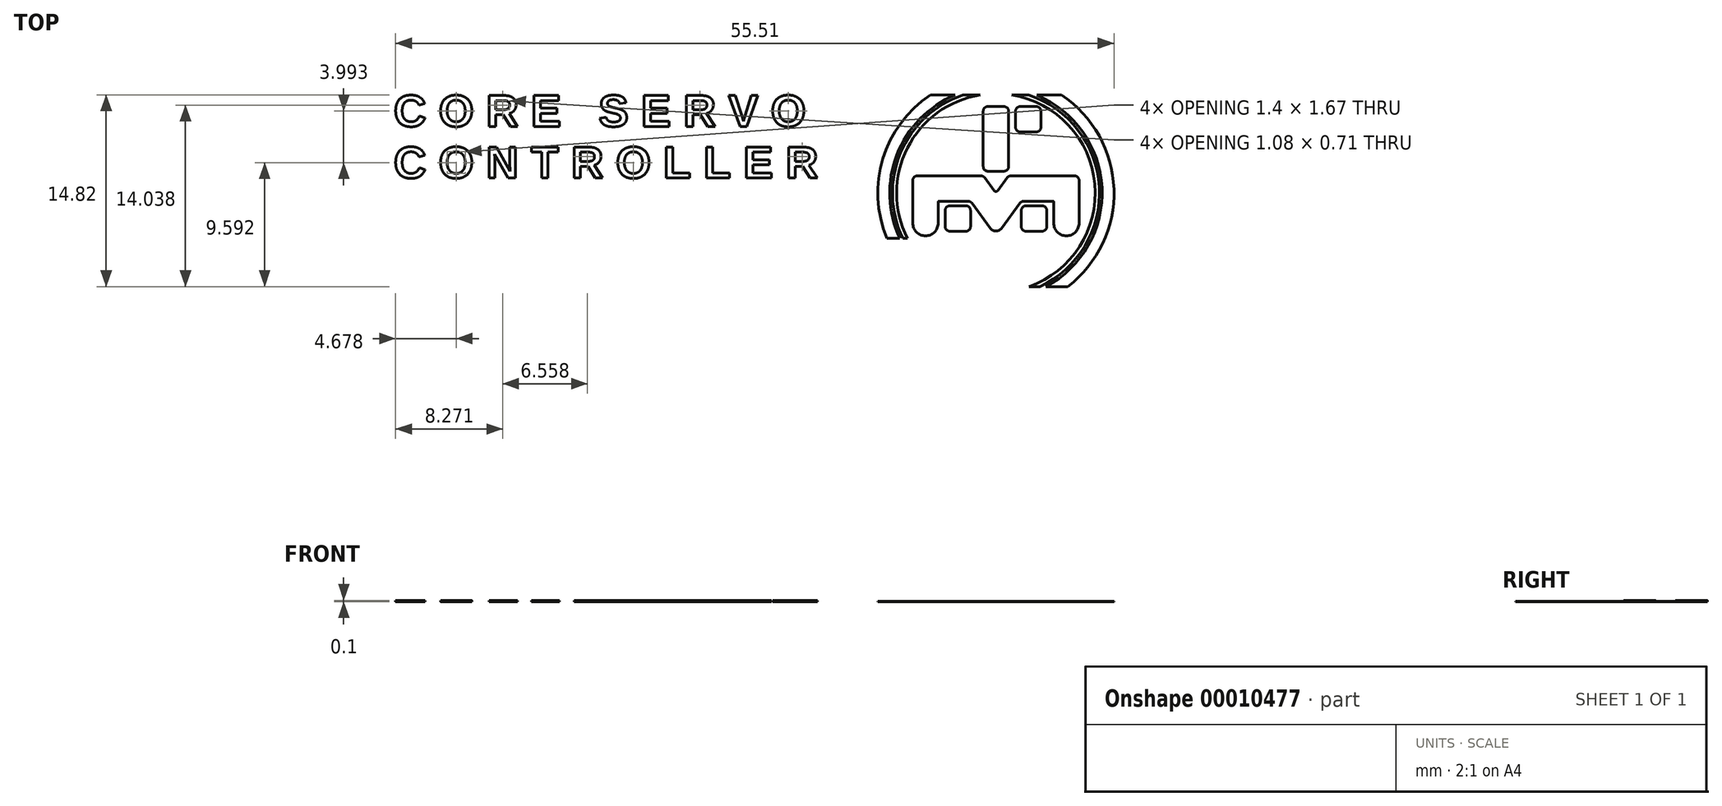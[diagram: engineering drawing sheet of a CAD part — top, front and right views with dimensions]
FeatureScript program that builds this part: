
annotation { "Feature Type Name" : "Feature", "Feature Type Description" : "" }
export const myFeature = defineFeature(function(context is Context, id is Id, definition is map)
    precondition{}
    {
        {
            var Q0;
            Q0=qCreatedBy(makeId("Top.planeOp"),FACE);
            var sketch = newSketch(context, id + "F0", { "sketchPlane" : qUnion([Q0])});
            skLineSegment(sketch, "E0.bottom", {"start": v(62.75, -5.5) * mm, "end": v(66.25, -5.5) * mm});
            skLineSegment(sketch, "E0.top", {"start": v(62.75, -19.5) * mm, "end": v(66.25, -19.5) * mm});
            skLineSegment(sketch, "E0.left", {"start": v(61.75, -6.5) * mm, "end": v(61.75, -18.5) * mm});
            skLineSegment(sketch, "E0.right", {"start": v(67.25, -6.5) * mm, "end": v(67.25, -18.5) * mm});
            skLineSegment(sketch, "E1.bottom", {"start": v(69.75, -5.5) * mm, "end": v(73.25, -5.5) * mm});
            skLineSegment(sketch, "E1.top", {"start": v(69.75, -11) * mm, "end": v(73.25, -11) * mm});
            skLineSegment(sketch, "E1.left", {"start": v(68.75, -6.5) * mm, "end": v(68.75, -10) * mm});
            skLineSegment(sketch, "E1.right", {"start": v(74.25, -6.5) * mm, "end": v(74.25, -10) * mm});
            skLineSegment(sketch, "E2", {"start": v(64.5, -19.5) * mm, "end": v(64.5, -33.5) * mm, "construction": true});
            skLineSegment(sketch, "E3", {"start": v(63.3, -31.86) * mm, "end": v(59.27, -26.4) * mm});
            skLineSegment(sketch, "E4", {"start": v(58.47, -26) * mm, "end": v(52.1, -26) * mm});
            skLineSegment(sketch, "E5", {"start": v(52, -26.1) * mm, "end": v(52, -30.75) * mm});
            skLineSegment(sketch, "E6.0", {"start": v(46.5, -21.5) * mm, "end": v(46.5, -30.75) * mm});
            skLineSegment(sketch, "E6.1", {"start": v(61.24, -20.5) * mm, "end": v(47.5, -20.5) * mm});
            skLineSegment(sketch, "E6.2", {"start": v(64.1, -23.68) * mm, "end": v(62.05, -20.9) * mm});
            skLineSegment(sketch, "E7", {"start": v(49.25, -33.5) * mm, "end": v(49.25, -33.5) * mm});
            skPoint(sketch, "E8.orphan", {"position": v(52, -33.5) * mm});
            skPoint(sketch, "E9.visualSharp", {"position": v(46.5, -33.5) * mm});
            skArc(sketch, "E9.filletArc", {"start": v(46.5, -30.75) * mm, "mid": v(47.3, -32.7) * mm, "end": v(49.25, -33.5) * mm});
            skArc(sketch, "E10.filletArc", {"start": v(49.25, -33.5) * mm, "mid": v(51.2, -32.7) * mm, "end": v(52, -30.75) * mm});
            skLineSegment(sketch, "E11.right", {"start": v(59, -28) * mm, "end": v(59, -31.5) * mm});
            skLineSegment(sketch, "E11.left", {"start": v(53.5, -28) * mm, "end": v(53.5, -31.5) * mm});
            skLineSegment(sketch, "E11.top", {"start": v(54.5, -32.5) * mm, "end": v(58, -32.5) * mm});
            skLineSegment(sketch, "E11.bottom", {"start": v(54.5, -27) * mm, "end": v(58, -27) * mm});
            skPoint(sketch, "E12.0.MirrorP", {"position": v(77, -33.5) * mm});
            skLineSegment(sketch, "E12.1.MirrorCS", {"start": v(74.5, -27) * mm, "end": v(71, -27) * mm});
            skPoint(sketch, "E12.2.MirrorP", {"position": v(82.5, -33.5) * mm});
            skLineSegment(sketch, "E12.3.MirrorCS", {"start": v(70, -28) * mm, "end": v(70, -31.5) * mm});
            skLineSegment(sketch, "E12.4.MirrorCS", {"start": v(75.5, -28) * mm, "end": v(75.5, -31.5) * mm});
            skLineSegment(sketch, "E12.5.MirrorCS", {"start": v(74.5, -32.5) * mm, "end": v(71, -32.5) * mm});
            skLineSegment(sketch, "E12.6.MirrorCS", {"start": v(70.53, -26) * mm, "end": v(76.9, -26) * mm});
            skLineSegment(sketch, "E12.7.MirrorCS", {"start": v(77, -26.1) * mm, "end": v(77, -30.75) * mm});
            skArc(sketch, "E12.8.MirrorCS", {"start": v(79.75, -33.5) * mm, "mid": v(77.8, -32.7) * mm, "end": v(77, -30.75) * mm});
            skLineSegment(sketch, "E12.9.MirrorCS", {"start": v(79.75, -33.5) * mm, "end": v(79.75, -33.5) * mm});
            skLineSegment(sketch, "E12.10.MirrorCS", {"start": v(67.76, -20.5) * mm, "end": v(81.5, -20.5) * mm});
            skPoint(sketch, "E12.11.MirrorP", {"position": v(77, -33.5) * mm});
            skLineSegment(sketch, "E12.12.MirrorCS", {"start": v(64.9, -23.68) * mm, "end": v(66.95, -20.9) * mm});
            skArc(sketch, "E12.13.MirrorCS", {"start": v(82.5, -30.75) * mm, "mid": v(81.7, -32.7) * mm, "end": v(79.75, -33.5) * mm});
            skLineSegment(sketch, "E12.14.MirrorCS", {"start": v(65.7, -31.86) * mm, "end": v(69.73, -26.4) * mm});
            skLineSegment(sketch, "E12.15.MirrorCS", {"start": v(82.5, -21.5) * mm, "end": v(82.5, -30.75) * mm});
            skPoint(sketch, "E13.visualSharp", {"position": v(68.75, -5.5) * mm});
            skArc(sketch, "E13.filletArc", {"start": v(69.75, -5.5) * mm, "mid": v(69.04, -5.8) * mm, "end": v(68.75, -6.5) * mm});
            skPoint(sketch, "E14.visualSharp", {"position": v(74.25, -5.5) * mm});
            skArc(sketch, "E14.filletArc", {"start": v(74.25, -6.5) * mm, "mid": v(73.96, -5.8) * mm, "end": v(73.25, -5.5) * mm});
            skPoint(sketch, "E15.visualSharp", {"position": v(74.25, -11) * mm});
            skArc(sketch, "E15.filletArc", {"start": v(73.25, -11) * mm, "mid": v(73.96, -10.7) * mm, "end": v(74.25, -10) * mm});
            skPoint(sketch, "E16.visualSharp", {"position": v(68.75, -11) * mm});
            skArc(sketch, "E16.filletArc", {"start": v(68.75, -10) * mm, "mid": v(69.04, -10.7) * mm, "end": v(69.75, -11) * mm});
            skPoint(sketch, "E17.visualSharp", {"position": v(67.25, -5.5) * mm});
            skArc(sketch, "E17.filletArc", {"start": v(67.25, -6.5) * mm, "mid": v(66.96, -5.8) * mm, "end": v(66.25, -5.5) * mm});
            skPoint(sketch, "E18.visualSharp", {"position": v(61.75, -5.5) * mm});
            skArc(sketch, "E18.filletArc", {"start": v(62.75, -5.5) * mm, "mid": v(62.04, -5.8) * mm, "end": v(61.75, -6.5) * mm});
            skPoint(sketch, "E19.visualSharp", {"position": v(61.75, -19.5) * mm});
            skArc(sketch, "E19.filletArc", {"start": v(61.75, -18.5) * mm, "mid": v(62.04, -19.2) * mm, "end": v(62.75, -19.5) * mm});
            skPoint(sketch, "E20.visualSharp", {"position": v(67.25, -19.5) * mm});
            skArc(sketch, "E20.filletArc", {"start": v(66.25, -19.5) * mm, "mid": v(66.96, -19.2) * mm, "end": v(67.25, -18.5) * mm});
            skPoint(sketch, "E21.visualSharp", {"position": v(70, -32.5) * mm});
            skArc(sketch, "E21.filletArc", {"start": v(70, -31.5) * mm, "mid": v(70.3, -32.2) * mm, "end": v(71, -32.5) * mm});
            skPoint(sketch, "E22.visualSharp", {"position": v(75.5, -27) * mm});
            skArc(sketch, "E22.filletArc", {"start": v(75.5, -28) * mm, "mid": v(75.2, -27.3) * mm, "end": v(74.5, -27) * mm});
            skPoint(sketch, "E23.visualSharp", {"position": v(70, -27) * mm});
            skArc(sketch, "E23.filletArc", {"start": v(71, -27) * mm, "mid": v(70.3, -27.3) * mm, "end": v(70, -28) * mm});
            skPoint(sketch, "E24.visualSharp", {"position": v(75.5, -32.5) * mm});
            skArc(sketch, "E24.filletArc", {"start": v(74.5, -32.5) * mm, "mid": v(75.2, -32.2) * mm, "end": v(75.5, -31.5) * mm});
            skPoint(sketch, "E25.visualSharp", {"position": v(59, -32.5) * mm});
            skArc(sketch, "E25.filletArc", {"start": v(58, -32.5) * mm, "mid": v(58.7, -32.2) * mm, "end": v(59, -31.5) * mm});
            skPoint(sketch, "E26.visualSharp", {"position": v(59, -27) * mm});
            skArc(sketch, "E26.filletArc", {"start": v(59, -28) * mm, "mid": v(58.7, -27.3) * mm, "end": v(58, -27) * mm});
            skPoint(sketch, "E27.visualSharp", {"position": v(53.5, -27) * mm});
            skArc(sketch, "E27.filletArc", {"start": v(54.5, -27) * mm, "mid": v(53.8, -27.3) * mm, "end": v(53.5, -28) * mm});
            skPoint(sketch, "E28.visualSharp", {"position": v(53.5, -32.5) * mm});
            skArc(sketch, "E28.filletArc", {"start": v(53.5, -31.5) * mm, "mid": v(53.8, -32.2) * mm, "end": v(54.5, -32.5) * mm});
            skPoint(sketch, "E29.visualSharp", {"position": v(46.5, -20.5) * mm});
            skArc(sketch, "E29.filletArc", {"start": v(47.5, -20.5) * mm, "mid": v(46.8, -20.8) * mm, "end": v(46.5, -21.5) * mm});
            skPoint(sketch, "E30.visualSharp", {"position": v(82.5, -20.5) * mm});
            skArc(sketch, "E30.filletArc", {"start": v(82.5, -21.5) * mm, "mid": v(82.2, -20.8) * mm, "end": v(81.5, -20.5) * mm});
            skPoint(sketch, "E31.visualSharp", {"position": v(61.75, -20.5) * mm});
            skArc(sketch, "E31.filletArc", {"start": v(62.05, -20.9) * mm, "mid": v(61.7, -20.6) * mm, "end": v(61.24, -20.5) * mm});
            skPoint(sketch, "E32.visualSharp", {"position": v(67.25, -20.5) * mm});
            skArc(sketch, "E32.filletArc", {"start": v(67.76, -20.5) * mm, "mid": v(67.3, -20.6) * mm, "end": v(66.95, -20.9) * mm});
            skPoint(sketch, "E33.visualSharp", {"position": v(52, -26) * mm});
            skArc(sketch, "E33.filletArc", {"start": v(52.1, -26) * mm, "mid": v(52.03, -26.03) * mm, "end": v(52, -26.1) * mm});
            skPoint(sketch, "E34.visualSharp", {"position": v(77, -26) * mm});
            skArc(sketch, "E34.filletArc", {"start": v(77, -26.1) * mm, "mid": v(76.97, -26.03) * mm, "end": v(76.9, -26) * mm});
            skPoint(sketch, "E35.visualSharp", {"position": v(70.03, -26) * mm});
            skArc(sketch, "E35.filletArc", {"start": v(70.53, -26) * mm, "mid": v(70.08, -26.1) * mm, "end": v(69.73, -26.4) * mm});
            skPoint(sketch, "E36.visualSharp", {"position": v(58.97, -26) * mm});
            skArc(sketch, "E36.filletArc", {"start": v(59.27, -26.4) * mm, "mid": v(58.92, -26.1) * mm, "end": v(58.47, -26) * mm});
            skPoint(sketch, "E37.visualSharp", {"position": v(64.5, -33.5) * mm});
            skArc(sketch, "E37.filletArc", {"start": v(63.3, -31.86) * mm, "mid": v(64.5, -32.47) * mm, "end": v(65.7, -31.86) * mm});
            skPoint(sketch, "E38.visualSharp", {"position": v(64.5, -24.23) * mm});
            skArc(sketch, "E38.filletArc", {"start": v(64.1, -23.68) * mm, "mid": v(64.5, -23.89) * mm, "end": v(64.9, -23.68) * mm});
            skArc(sketch, "E39", {"start": v(71.68, -44.5) * mm, "mid": v(85.92, -22.29) * mm, "end": v(67.92, -3) * mm});
            skArc(sketch, "E40", {"start": v(74, -44.5) * mm, "mid": v(86.85, -22.94) * mm, "end": v(71.6, -3) * mm});
            skArc(sketch, "E41", {"start": v(75.35, -44.5) * mm, "mid": v(87.46, -23.1) * mm, "end": v(73.32, -3) * mm});
            skArc(sketch, "E42", {"start": v(80.06, -44.5) * mm, "mid": v(90.04, -23.4) * mm, "end": v(78.72, -3) * mm});
            skLineSegment(sketch, "E43", {"start": v(80.06, -44.5) * mm, "end": v(75.35, -44.5) * mm});
            skLineSegment(sketch, "E44.trimOffspring", {"start": v(74, -44.5) * mm, "end": v(71.68, -44.5) * mm});
            skLineSegment(sketch, "E45", {"start": v(40.9, -34) * mm, "end": v(43.69, -34) * mm});
            skLineSegment(sketch, "E46.trimOffspring", {"start": v(44.36, -34) * mm, "end": v(45.34, -34) * mm});
            skLineSegment(sketch, "E47", {"start": v(50.28, -3) * mm, "end": v(55.68, -3) * mm});
            skArc(sketch, "E48.trimOffspring", {"start": v(61.08, -3) * mm, "mid": v(45.33, -14.5) * mm, "end": v(45.34, -34) * mm});
            skArc(sketch, "E49.trimOffspring", {"start": v(50.28, -3) * mm, "mid": v(40.05, -16.82) * mm, "end": v(40.9, -34) * mm});
            skArc(sketch, "E50.trimOffspring", {"start": v(55.68, -3) * mm, "mid": v(43.06, -15.94) * mm, "end": v(43.69, -34) * mm});
            skArc(sketch, "E51.trimOffspring", {"start": v(57.4, -3) * mm, "mid": v(43.86, -15.55) * mm, "end": v(44.36, -34) * mm});
            skLineSegment(sketch, "E52.trimOffspring", {"start": v(67.92, -3) * mm, "end": v(71.6, -3) * mm});
            skLineSegment(sketch, "E53.trimOffspring", {"start": v(57.4, -3) * mm, "end": v(61.08, -3) * mm});
            skLineSegment(sketch, "E54.trimOffspring", {"start": v(73.32, -3) * mm, "end": v(78.72, -3) * mm});
            skSolve(sketch);
        }
        {
            var Q0;
            Q0=makeQuery(id+"F0.imprint","IMPRINT",FACE,{"disambiguationData":[TD([[makeQuery(id+"F0.imprint","IMPRINT",EDGE,{"derivedFrom":sQuery(id+"F0.wireOp",EDGE,"46c11c21-c6ca-42b8-9659-15b4f280ee3c.sketch_text.stroke-197")}),1.0]])]});
            var Q1;
            Q1=makeQuery(id+"F0.imprint","IMPRINT",FACE,{"disambiguationData":[TD([[makeQuery(id+"F0.imprint","IMPRINT",EDGE,{"derivedFrom":sQuery(id+"F0.wireOp",EDGE,"E1.bottom")}),-1.0]])]});
            var Q2;
            Q2=makeQuery(id+"F0.imprint","IMPRINT",FACE,{"disambiguationData":[TD([[makeQuery(id+"F0.imprint","IMPRINT",EDGE,{"derivedFrom":sQuery(id+"F0.wireOp",EDGE,"46c11c21-c6ca-42b8-9659-15b4f280ee3c.sketch_text.stroke-126")}),-1.0]])]});
            var Q3;
            Q3=makeQuery(id+"F0.imprint","IMPRINT",FACE,{"disambiguationData":[TD([[makeQuery(id+"F0.imprint","IMPRINT",EDGE,{"derivedFrom":sQuery(id+"F0.wireOp",EDGE,"46c11c21-c6ca-42b8-9659-15b4f280ee3c.sketch_text.stroke-360")}),-1.0]])]});
            var Q4;
            Q4=makeQuery(id+"F0.imprint","IMPRINT",FACE,{"disambiguationData":[TD([[makeQuery(id+"F0.imprint","IMPRINT",EDGE,{"derivedFrom":sQuery(id+"F0.wireOp",EDGE,"E0.bottom")}),-1.0]])]});
            var Q5;
            Q5=makeQuery(id+"F0.imprint","IMPRINT",FACE,{"disambiguationData":[TD([[makeQuery(id+"F0.imprint","IMPRINT",EDGE,{"derivedFrom":sQuery(id+"F0.wireOp",EDGE,"46c11c21-c6ca-42b8-9659-15b4f280ee3c.sketch_text.stroke-0")}),-1.0]])]});
            var Q6;
            Q6=makeQuery(id+"F0.imprint","IMPRINT",FACE,{"disambiguationData":[TD([[makeQuery(id+"F0.imprint","IMPRINT",EDGE,{"derivedFrom":sQuery(id+"F0.wireOp",EDGE,"46c11c21-c6ca-42b8-9659-15b4f280ee3c.sketch_text.stroke-90")}),-1.0]])]});
            var Q7;
            Q7=makeQuery(id+"F0.imprint","IMPRINT",FACE,{"disambiguationData":[TD([[makeQuery(id+"F0.imprint","IMPRINT",EDGE,{"derivedFrom":sQuery(id+"F0.wireOp",EDGE,"46c11c21-c6ca-42b8-9659-15b4f280ee3c.sketch_text.stroke-145")}),-1.0]])]});
            var Q8;
            Q8=makeQuery(id+"F0.imprint","IMPRINT",FACE,{"disambiguationData":[TD([[makeQuery(id+"F0.imprint","IMPRINT",EDGE,{"derivedFrom":sQuery(id+"F0.wireOp",EDGE,"46c11c21-c6ca-42b8-9659-15b4f280ee3c.sketch_text.stroke-126")}),1.0]])]});
            var Q9;
            Q9=makeQuery(id+"F0.imprint","IMPRINT",FACE,{"disambiguationData":[TD([[makeQuery(id+"F0.imprint","IMPRINT",EDGE,{"derivedFrom":sQuery(id+"F0.wireOp",EDGE,"46c11c21-c6ca-42b8-9659-15b4f280ee3c.sketch_text.stroke-48")}),-1.0]])]});
            var Q10;
            Q10=makeQuery(id+"F0.imprint","IMPRINT",FACE,{"disambiguationData":[TD([[makeQuery(id+"F0.imprint","IMPRINT",EDGE,{"derivedFrom":sQuery(id+"F0.wireOp",EDGE,"46c11c21-c6ca-42b8-9659-15b4f280ee3c.sketch_text.stroke-239")}),1.0]])]});
            var Q11;
            Q11=makeQuery(id+"F0.imprint","IMPRINT",FACE,{"disambiguationData":[TD([[makeQuery(id+"F0.imprint","IMPRINT",EDGE,{"derivedFrom":sQuery(id+"F0.wireOp",EDGE,"E12.1.MirrorCS")}),1.0]])]});
            var Q12;
            Q12=makeQuery(id+"F0.imprint","IMPRINT",FACE,{"disambiguationData":[TD([[makeQuery(id+"F0.imprint","IMPRINT",EDGE,{"derivedFrom":sQuery(id+"F0.wireOp",EDGE,"46c11c21-c6ca-42b8-9659-15b4f280ee3c.sketch_text.stroke-300")}),-1.0]])]});
            var Q13;
            Q13=makeQuery(id+"F0.imprint","IMPRINT",FACE,{"disambiguationData":[TD([[makeQuery(id+"F0.imprint","IMPRINT",EDGE,{"derivedFrom":sQuery(id+"F0.wireOp",EDGE,"46c11c21-c6ca-42b8-9659-15b4f280ee3c.sketch_text.stroke-245")}),-1.0]])]});
            var Q14;
            Q14=makeQuery(id+"F0.imprint","IMPRINT",FACE,{"disambiguationData":[TD([[makeQuery(id+"F0.imprint","IMPRINT",EDGE,{"derivedFrom":sQuery(id+"F0.wireOp",EDGE,"46c11c21-c6ca-42b8-9659-15b4f280ee3c.sketch_text.stroke-268")}),-1.0]])]});
            var Q15;
            Q15=makeQuery(id+"F0.imprint","IMPRINT",FACE,{"disambiguationData":[TD([[makeQuery(id+"F0.imprint","IMPRINT",EDGE,{"derivedFrom":sQuery(id+"F0.wireOp",EDGE,"46c11c21-c6ca-42b8-9659-15b4f280ee3c.sketch_text.stroke-189")}),-1.0]])]});
            var Q16;
            Q16=makeQuery(id+"F0.imprint","IMPRINT",FACE,{"disambiguationData":[TD([[makeQuery(id+"F0.imprint","IMPRINT",EDGE,{"derivedFrom":sQuery(id+"F0.wireOp",EDGE,"46c11c21-c6ca-42b8-9659-15b4f280ee3c.sketch_text.stroke-114")}),-1.0]])]});
            var Q17;
            Q17=makeQuery(id+"F0.imprint","IMPRINT",FACE,{"disambiguationData":[TD([[makeQuery(id+"F0.imprint","IMPRINT",EDGE,{"derivedFrom":sQuery(id+"F0.wireOp",EDGE,"E3")}),-1.0]])]});
            var Q18;
            Q18=makeQuery(id+"F0.imprint","IMPRINT",FACE,{"disambiguationData":[TD([[makeQuery(id+"F0.imprint","IMPRINT",EDGE,{"derivedFrom":sQuery(id+"F0.wireOp",EDGE,"46c11c21-c6ca-42b8-9659-15b4f280ee3c.sketch_text.stroke-345")}),-1.0]])]});
            var Q19;
            Q19=makeQuery(id+"F0.imprint","IMPRINT",FACE,{"disambiguationData":[TD([[makeQuery(id+"F0.imprint","IMPRINT",EDGE,{"derivedFrom":sQuery(id+"F0.wireOp",EDGE,"46c11c21-c6ca-42b8-9659-15b4f280ee3c.sketch_text.stroke-232")}),1.0]])]});
            var Q20;
            Q20=makeQuery(id+"F0.imprint","IMPRINT",FACE,{"disambiguationData":[TD([[makeQuery(id+"F0.imprint","IMPRINT",EDGE,{"derivedFrom":sQuery(id+"F0.wireOp",EDGE,"46c11c21-c6ca-42b8-9659-15b4f280ee3c.sketch_text.stroke-280")}),1.0]])]});
            var Q21;
            Q21=makeQuery(id+"F0.imprint","IMPRINT",FACE,{"disambiguationData":[TD([[makeQuery(id+"F0.imprint","IMPRINT",EDGE,{"derivedFrom":sQuery(id+"F0.wireOp",EDGE,"46c11c21-c6ca-42b8-9659-15b4f280ee3c.sketch_text.stroke-161")}),-1.0]])]});
            var Q22;
            Q22=makeQuery(id+"F0.imprint","IMPRINT",FACE,{"disambiguationData":[TD([[makeQuery(id+"F0.imprint","IMPRINT",EDGE,{"derivedFrom":sQuery(id+"F0.wireOp",EDGE,"46c11c21-c6ca-42b8-9659-15b4f280ee3c.sketch_text.stroke-157")}),-1.0]])]});
            var Q23;
            Q23=makeQuery(id+"F0.imprint","IMPRINT",FACE,{"disambiguationData":[TD([[makeQuery(id+"F0.imprint","IMPRINT",EDGE,{"derivedFrom":sQuery(id+"F0.wireOp",EDGE,"46c11c21-c6ca-42b8-9659-15b4f280ee3c.sketch_text.stroke-84")}),1.0]])]});
            var Q24;
            Q24=makeQuery(id+"F0.imprint","IMPRINT",FACE,{"disambiguationData":[TD([[makeQuery(id+"F0.imprint","IMPRINT",EDGE,{"derivedFrom":sQuery(id+"F0.wireOp",EDGE,"46c11c21-c6ca-42b8-9659-15b4f280ee3c.sketch_text.stroke-60")}),-1.0]])]});
            var Q25;
            Q25=makeQuery(id+"F0.imprint","IMPRINT",FACE,{"disambiguationData":[TD([[makeQuery(id+"F0.imprint","IMPRINT",EDGE,{"derivedFrom":sQuery(id+"F0.wireOp",EDGE,"46c11c21-c6ca-42b8-9659-15b4f280ee3c.sketch_text.stroke-340")}),1.0]])]});
            var Q26;
            Q26=makeQuery(id+"F0.imprint","IMPRINT",FACE,{"disambiguationData":[TD([[makeQuery(id+"F0.imprint","IMPRINT",EDGE,{"derivedFrom":sQuery(id+"F0.wireOp",EDGE,"46c11c21-c6ca-42b8-9659-15b4f280ee3c.sketch_text.stroke-220")}),-1.0]])]});
            var Q27;
            Q27=makeQuery(id+"F0.imprint","IMPRINT",FACE,{"disambiguationData":[TD([[makeQuery(id+"F0.imprint","IMPRINT",EDGE,{"derivedFrom":sQuery(id+"F0.wireOp",EDGE,"46c11c21-c6ca-42b8-9659-15b4f280ee3c.sketch_text.stroke-76")}),-1.0]])]});
            var Q28;
            Q28=makeQuery(id+"F0.imprint","IMPRINT",FACE,{"disambiguationData":[TD([[makeQuery(id+"F0.imprint","IMPRINT",EDGE,{"derivedFrom":sQuery(id+"F0.wireOp",EDGE,"46c11c21-c6ca-42b8-9659-15b4f280ee3c.sketch_text.stroke-327")}),1.0]])]});
            var Q29;
            Q29=makeQuery(id+"F0.imprint","IMPRINT",FACE,{"disambiguationData":[TD([[makeQuery(id+"F0.imprint","IMPRINT",EDGE,{"derivedFrom":sQuery(id+"F0.wireOp",EDGE,"46c11c21-c6ca-42b8-9659-15b4f280ee3c.sketch_text.stroke-29")}),-1.0]])]});
            var Q30;
            Q30=makeQuery(id+"F0.imprint","IMPRINT",FACE,{"disambiguationData":[TD([[makeQuery(id+"F0.imprint","IMPRINT",EDGE,{"derivedFrom":sQuery(id+"F0.wireOp",EDGE,"46c11c21-c6ca-42b8-9659-15b4f280ee3c.sketch_text.stroke-60")}),1.0]])]});
            var Q31;
            Q31=makeQuery(id+"F0.imprint","IMPRINT",FACE,{"disambiguationData":[TD([[makeQuery(id+"F0.imprint","IMPRINT",EDGE,{"derivedFrom":sQuery(id+"F0.wireOp",EDGE,"46c11c21-c6ca-42b8-9659-15b4f280ee3c.sketch_text.stroke-333")}),-1.0]])]});
            var Q32;
            Q32=makeQuery(id+"F0.imprint","IMPRINT",FACE,{"disambiguationData":[TD([[makeQuery(id+"F0.imprint","IMPRINT",EDGE,{"derivedFrom":sQuery(id+"F0.wireOp",EDGE,"E11.right")}),-1.0]])]});
            var Q33;
            Q33=makeQuery(id+"F0.imprint","IMPRINT",FACE,{"disambiguationData":[TD([[makeQuery(id+"F0.imprint","IMPRINT",EDGE,{"derivedFrom":sQuery(id+"F0.wireOp",EDGE,"46c11c21-c6ca-42b8-9659-15b4f280ee3c.sketch_text.stroke-216")}),-1.0]])]});
            var Q34;
            Q34=makeQuery(id+"F0.imprint","IMPRINT",FACE,{"disambiguationData":[TD([[makeQuery(id+"F0.imprint","IMPRINT",EDGE,{"derivedFrom":sQuery(id+"F0.wireOp",EDGE,"46c11c21-c6ca-42b8-9659-15b4f280ee3c.sketch_text.stroke-260")}),-1.0]])]});
            var Q35;
            Q35=makeQuery(id+"F0.imprint","IMPRINT",FACE,{"disambiguationData":[TD([[makeQuery(id+"F0.imprint","IMPRINT",EDGE,{"derivedFrom":sQuery(id+"F0.wireOp",EDGE,"46c11c21-c6ca-42b8-9659-15b4f280ee3c.sketch_text.stroke-286")}),-1.0]])]});
            var Q36;
            Q36=makeQuery(id+"F0.imprint","IMPRINT",FACE,{"disambiguationData":[TD([[makeQuery(id+"F0.imprint","IMPRINT",EDGE,{"derivedFrom":sQuery(id+"F0.wireOp",EDGE,"46c11c21-c6ca-42b8-9659-15b4f280ee3c.sketch_text.stroke-197")}),-1.0]])]});
            var Q37;
            Q37=makeQuery(id+"F0.imprint","IMPRINT",FACE,{"disambiguationData":[TD([[makeQuery(id+"F0.imprint","IMPRINT",EDGE,{"derivedFrom":sQuery(id+"F0.wireOp",EDGE,"46c11c21-c6ca-42b8-9659-15b4f280ee3c.sketch_text.stroke-319")}),-1.0]])]});
            var Q38;
            Q38=makeQuery(id+"F0.imprint","IMPRINT",FACE,{"disambiguationData":[TD([[makeQuery(id+"F0.imprint","IMPRINT",EDGE,{"derivedFrom":sQuery(id+"F0.wireOp",EDGE,"46c11c21-c6ca-42b8-9659-15b4f280ee3c.sketch_text.stroke-366")}),-1.0]])]});
            var Q39;
            Q39=makeQuery(id+"F0.imprint","IMPRINT",FACE,{"disambiguationData":[TD([[makeQuery(id+"F0.imprint","IMPRINT",EDGE,{"derivedFrom":sQuery(id+"F0.wireOp",EDGE,"46c11c21-c6ca-42b8-9659-15b4f280ee3c.sketch_text.stroke-272")}),-1.0]])]});
            var Q40;
            Q40=makeQuery(id+"F0.imprint","IMPRINT",FACE,{"disambiguationData":[TD([[makeQuery(id+"F0.imprint","IMPRINT",EDGE,{"derivedFrom":sQuery(id+"F0.wireOp",EDGE,"46c11c21-c6ca-42b8-9659-15b4f280ee3c.sketch_text.stroke-15")}),-1.0]])]});
            var Q41;
            Q41=makeQuery(id+"F0.imprint","IMPRINT",FACE,{"disambiguationData":[TD([[makeQuery(id+"F0.imprint","IMPRINT",EDGE,{"derivedFrom":sQuery(id+"F0.wireOp",EDGE,"46c11c21-c6ca-42b8-9659-15b4f280ee3c.sketch_text.stroke-168")}),-1.0]])]});
            var Q42;
            Q42=makeQuery(id+"F0.imprint","IMPRINT",FACE,{"disambiguationData":[TD([[makeQuery(id+"F0.imprint","IMPRINT",EDGE,{"derivedFrom":sQuery(id+"F0.wireOp",EDGE,"46c11c21-c6ca-42b8-9659-15b4f280ee3c.sketch_text.stroke-95")}),-1.0]])]});
            var Q43;
            Q43=makeQuery(id+"F0.imprint","IMPRINT",FACE,{"disambiguationData":[TD([[makeQuery(id+"F0.imprint","IMPRINT",EDGE,{"derivedFrom":sQuery(id+"F0.wireOp",EDGE,"46c11c21-c6ca-42b8-9659-15b4f280ee3c.sketch_text.stroke-225")}),-1.0]])]});
            var Q44;
            Q44=makeQuery(id+"F0.imprint","IMPRINT",FACE,{"disambiguationData":[TD([[makeQuery(id+"F0.imprint","IMPRINT",EDGE,{"derivedFrom":sQuery(id+"F0.wireOp",EDGE,"46c11c21-c6ca-42b8-9659-15b4f280ee3c.sketch_text.stroke-231")}),-1.0]])]});
            var Q45;
            Q45=makeQuery(id+"F0.imprint","IMPRINT",FACE,{"disambiguationData":[TD([[makeQuery(id+"F0.imprint","IMPRINT",EDGE,{"derivedFrom":sQuery(id+"F0.wireOp",EDGE,"46c11c21-c6ca-42b8-9659-15b4f280ee3c.sketch_text.stroke-177")}),-1.0]])]});
            var Q46;
            Q46=makeQuery(id+"F0.imprint","IMPRINT",FACE,{"disambiguationData":[TD([[makeQuery(id+"F0.imprint","IMPRINT",EDGE,{"derivedFrom":sQuery(id+"F0.wireOp",EDGE,"E41")}),-1.0]])]});
            var Q47;
            Q47=makeQuery(id+"F0.imprint","IMPRINT",FACE,{"disambiguationData":[TD([[makeQuery(id+"F0.imprint","IMPRINT",EDGE,{"derivedFrom":sQuery(id+"F0.wireOp",EDGE,"E39")}),-1.0]])]});
            var Q48;
            Q48=makeQuery(id+"F0.imprint","IMPRINT",FACE,{"disambiguationData":[TD([[makeQuery(id+"F0.imprint","IMPRINT",EDGE,{"derivedFrom":sQuery(id+"F0.wireOp",EDGE,"E45")}),1.0]])]});
            var Q49;
            Q49=makeQuery(id+"F0.imprint","IMPRINT",FACE,{"disambiguationData":[TD([[makeQuery(id+"F0.imprint","IMPRINT",EDGE,{"derivedFrom":sQuery(id+"F0.wireOp",EDGE,"E46.trimOffspring")}),1.0]])]});
            extrude(context, id + "F1", {"entities" : qUnion([Q0, Q1, Q2, Q3, Q4, Q5, Q6, Q7, Q8, Q9, Q10, Q11, Q12, Q13, Q14, Q15, Q16, Q17, Q18, Q19, Q20, Q21, Q22, Q23, Q24, Q25, Q26, Q27, Q28, Q29, Q30, Q31, Q32, Q33, Q34, Q35, Q36, Q37, Q38, Q39, Q40, Q41, Q42, Q43, Q44, Q45, Q46, Q47, Q48, Q49]), "depth" : .1 * mm});
        }
        {
            var Q0;
            Q0=makeQuery(id+"F1.opExtrude","SWEPT_BODY",BODY,{"disambiguationData":[OSD([sQuery(id+"F0.wireOp",EDGE,"46c11c21-c6ca-42b8-9659-15b4f280ee3c.sketch_text.stroke-149"),sQuery(id+"F0.wireOp",EDGE,"46c11c21-c6ca-42b8-9659-15b4f280ee3c.sketch_text.stroke-150"),sQuery(id+"F0.wireOp",EDGE,"46c11c21-c6ca-42b8-9659-15b4f280ee3c.sketch_text.stroke-151"),sQuery(id+"F0.wireOp",EDGE,"46c11c21-c6ca-42b8-9659-15b4f280ee3c.sketch_text.stroke-152"),sQuery(id+"F0.wireOp",EDGE,"46c11c21-c6ca-42b8-9659-15b4f280ee3c.sketch_text.stroke-153"),sQuery(id+"F0.wireOp",EDGE,"46c11c21-c6ca-42b8-9659-15b4f280ee3c.sketch_text.stroke-154"),sQuery(id+"F0.wireOp",EDGE,"46c11c21-c6ca-42b8-9659-15b4f280ee3c.sketch_text.stroke-155"),sQuery(id+"F0.wireOp",EDGE,"46c11c21-c6ca-42b8-9659-15b4f280ee3c.sketch_text.stroke-156"),sQuery(id+"F0.wireOp",EDGE,"46c11c21-c6ca-42b8-9659-15b4f280ee3c.sketch_text.stroke-157"),sQuery(id+"F0.wireOp",EDGE,"46c11c21-c6ca-42b8-9659-15b4f280ee3c.sketch_text.stroke-158"),sQuery(id+"F0.wireOp",EDGE,"46c11c21-c6ca-42b8-9659-15b4f280ee3c.sketch_text.stroke-159"),sQuery(id+"F0.wireOp",EDGE,"46c11c21-c6ca-42b8-9659-15b4f280ee3c.sketch_text.stroke-160"),sQuery(id+"F0.wireOp",EDGE,"46c11c21-c6ca-42b8-9659-15b4f280ee3c.sketch_text.stroke-161"),sQuery(id+"F0.wireOp",EDGE,"46c11c21-c6ca-42b8-9659-15b4f280ee3c.sketch_text.stroke-162")])]});
            var Q1;
            Q1=makeQuery(id+"F1.opExtrude","SWEPT_BODY",BODY,{"disambiguationData":[OSD([sQuery(id+"F0.wireOp",EDGE,"46c11c21-c6ca-42b8-9659-15b4f280ee3c.sketch_text.stroke-134"),sQuery(id+"F0.wireOp",EDGE,"46c11c21-c6ca-42b8-9659-15b4f280ee3c.sketch_text.stroke-135"),sQuery(id+"F0.wireOp",EDGE,"46c11c21-c6ca-42b8-9659-15b4f280ee3c.sketch_text.stroke-136"),sQuery(id+"F0.wireOp",EDGE,"46c11c21-c6ca-42b8-9659-15b4f280ee3c.sketch_text.stroke-137"),sQuery(id+"F0.wireOp",EDGE,"46c11c21-c6ca-42b8-9659-15b4f280ee3c.sketch_text.stroke-138"),sQuery(id+"F0.wireOp",EDGE,"46c11c21-c6ca-42b8-9659-15b4f280ee3c.sketch_text.stroke-139"),sQuery(id+"F0.wireOp",EDGE,"46c11c21-c6ca-42b8-9659-15b4f280ee3c.sketch_text.stroke-140"),sQuery(id+"F0.wireOp",EDGE,"46c11c21-c6ca-42b8-9659-15b4f280ee3c.sketch_text.stroke-141"),sQuery(id+"F0.wireOp",EDGE,"46c11c21-c6ca-42b8-9659-15b4f280ee3c.sketch_text.stroke-142"),sQuery(id+"F0.wireOp",EDGE,"46c11c21-c6ca-42b8-9659-15b4f280ee3c.sketch_text.stroke-143"),sQuery(id+"F0.wireOp",EDGE,"46c11c21-c6ca-42b8-9659-15b4f280ee3c.sketch_text.stroke-144"),sQuery(id+"F0.wireOp",EDGE,"46c11c21-c6ca-42b8-9659-15b4f280ee3c.sketch_text.stroke-145"),sQuery(id+"F0.wireOp",EDGE,"46c11c21-c6ca-42b8-9659-15b4f280ee3c.sketch_text.stroke-146"),sQuery(id+"F0.wireOp",EDGE,"46c11c21-c6ca-42b8-9659-15b4f280ee3c.sketch_text.stroke-147"),sQuery(id+"F0.wireOp",EDGE,"46c11c21-c6ca-42b8-9659-15b4f280ee3c.sketch_text.stroke-148")])]});
            var Q2;
            Q2=makeQuery(id+"F1.opExtrude","SWEPT_BODY",BODY,{"disambiguationData":[OSD([sQuery(id+"F0.wireOp",EDGE,"46c11c21-c6ca-42b8-9659-15b4f280ee3c.sketch_text.stroke-101"),sQuery(id+"F0.wireOp",EDGE,"46c11c21-c6ca-42b8-9659-15b4f280ee3c.sketch_text.stroke-102"),sQuery(id+"F0.wireOp",EDGE,"46c11c21-c6ca-42b8-9659-15b4f280ee3c.sketch_text.stroke-103"),sQuery(id+"F0.wireOp",EDGE,"46c11c21-c6ca-42b8-9659-15b4f280ee3c.sketch_text.stroke-104"),sQuery(id+"F0.wireOp",EDGE,"46c11c21-c6ca-42b8-9659-15b4f280ee3c.sketch_text.stroke-105"),sQuery(id+"F0.wireOp",EDGE,"46c11c21-c6ca-42b8-9659-15b4f280ee3c.sketch_text.stroke-106"),sQuery(id+"F0.wireOp",EDGE,"46c11c21-c6ca-42b8-9659-15b4f280ee3c.sketch_text.stroke-107"),sQuery(id+"F0.wireOp",EDGE,"46c11c21-c6ca-42b8-9659-15b4f280ee3c.sketch_text.stroke-108"),sQuery(id+"F0.wireOp",EDGE,"46c11c21-c6ca-42b8-9659-15b4f280ee3c.sketch_text.stroke-109"),sQuery(id+"F0.wireOp",EDGE,"46c11c21-c6ca-42b8-9659-15b4f280ee3c.sketch_text.stroke-110"),sQuery(id+"F0.wireOp",EDGE,"46c11c21-c6ca-42b8-9659-15b4f280ee3c.sketch_text.stroke-111"),sQuery(id+"F0.wireOp",EDGE,"46c11c21-c6ca-42b8-9659-15b4f280ee3c.sketch_text.stroke-112"),sQuery(id+"F0.wireOp",EDGE,"46c11c21-c6ca-42b8-9659-15b4f280ee3c.sketch_text.stroke-113"),sQuery(id+"F0.wireOp",EDGE,"46c11c21-c6ca-42b8-9659-15b4f280ee3c.sketch_text.stroke-114")])]});
            var Q3;
            Q3=makeQuery(id+"F1.opExtrude","SWEPT_BODY",BODY,{"disambiguationData":[OSD([sQuery(id+"F0.wireOp",EDGE,"46c11c21-c6ca-42b8-9659-15b4f280ee3c.sketch_text.stroke-79"),sQuery(id+"F0.wireOp",EDGE,"46c11c21-c6ca-42b8-9659-15b4f280ee3c.sketch_text.stroke-80"),sQuery(id+"F0.wireOp",EDGE,"46c11c21-c6ca-42b8-9659-15b4f280ee3c.sketch_text.stroke-81"),sQuery(id+"F0.wireOp",EDGE,"46c11c21-c6ca-42b8-9659-15b4f280ee3c.sketch_text.stroke-82"),sQuery(id+"F0.wireOp",EDGE,"46c11c21-c6ca-42b8-9659-15b4f280ee3c.sketch_text.stroke-83"),sQuery(id+"F0.wireOp",EDGE,"46c11c21-c6ca-42b8-9659-15b4f280ee3c.sketch_text.stroke-84"),sQuery(id+"F0.wireOp",EDGE,"46c11c21-c6ca-42b8-9659-15b4f280ee3c.sketch_text.stroke-85"),sQuery(id+"F0.wireOp",EDGE,"46c11c21-c6ca-42b8-9659-15b4f280ee3c.sketch_text.stroke-86"),sQuery(id+"F0.wireOp",EDGE,"46c11c21-c6ca-42b8-9659-15b4f280ee3c.sketch_text.stroke-87"),sQuery(id+"F0.wireOp",EDGE,"46c11c21-c6ca-42b8-9659-15b4f280ee3c.sketch_text.stroke-88"),sQuery(id+"F0.wireOp",EDGE,"46c11c21-c6ca-42b8-9659-15b4f280ee3c.sketch_text.stroke-89"),sQuery(id+"F0.wireOp",EDGE,"46c11c21-c6ca-42b8-9659-15b4f280ee3c.sketch_text.stroke-90"),sQuery(id+"F0.wireOp",EDGE,"46c11c21-c6ca-42b8-9659-15b4f280ee3c.sketch_text.stroke-91"),sQuery(id+"F0.wireOp",EDGE,"46c11c21-c6ca-42b8-9659-15b4f280ee3c.sketch_text.stroke-92")])]});
            var Q4;
            Q4=makeQuery(id+"F1.opExtrude","SWEPT_BODY",BODY,{"disambiguationData":[OSD([sQuery(id+"F0.wireOp",EDGE,"E0.bottom"),sQuery(id+"F0.wireOp",EDGE,"E0.top"),sQuery(id+"F0.wireOp",EDGE,"E0.left"),sQuery(id+"F0.wireOp",EDGE,"E0.right"),sQuery(id+"F0.wireOp",EDGE,"E17.filletArc"),sQuery(id+"F0.wireOp",EDGE,"E18.filletArc"),sQuery(id+"F0.wireOp",EDGE,"E19.filletArc"),sQuery(id+"F0.wireOp",EDGE,"E20.filletArc")])]});
            var Q5;
            Q5=makeQuery(id+"F1.opExtrude","SWEPT_BODY",BODY,{"disambiguationData":[OSD([sQuery(id+"F0.wireOp",EDGE,"46c11c21-c6ca-42b8-9659-15b4f280ee3c.sketch_text.stroke-242"),sQuery(id+"F0.wireOp",EDGE,"46c11c21-c6ca-42b8-9659-15b4f280ee3c.sketch_text.stroke-243"),sQuery(id+"F0.wireOp",EDGE,"46c11c21-c6ca-42b8-9659-15b4f280ee3c.sketch_text.stroke-244"),sQuery(id+"F0.wireOp",EDGE,"46c11c21-c6ca-42b8-9659-15b4f280ee3c.sketch_text.stroke-245"),sQuery(id+"F0.wireOp",EDGE,"46c11c21-c6ca-42b8-9659-15b4f280ee3c.sketch_text.stroke-246"),sQuery(id+"F0.wireOp",EDGE,"46c11c21-c6ca-42b8-9659-15b4f280ee3c.sketch_text.stroke-247"),sQuery(id+"F0.wireOp",EDGE,"46c11c21-c6ca-42b8-9659-15b4f280ee3c.sketch_text.stroke-248"),sQuery(id+"F0.wireOp",EDGE,"46c11c21-c6ca-42b8-9659-15b4f280ee3c.sketch_text.stroke-249"),sQuery(id+"F0.wireOp",EDGE,"46c11c21-c6ca-42b8-9659-15b4f280ee3c.sketch_text.stroke-250"),sQuery(id+"F0.wireOp",EDGE,"46c11c21-c6ca-42b8-9659-15b4f280ee3c.sketch_text.stroke-251"),sQuery(id+"F0.wireOp",EDGE,"46c11c21-c6ca-42b8-9659-15b4f280ee3c.sketch_text.stroke-252"),sQuery(id+"F0.wireOp",EDGE,"46c11c21-c6ca-42b8-9659-15b4f280ee3c.sketch_text.stroke-253"),sQuery(id+"F0.wireOp",EDGE,"46c11c21-c6ca-42b8-9659-15b4f280ee3c.sketch_text.stroke-254"),sQuery(id+"F0.wireOp",EDGE,"46c11c21-c6ca-42b8-9659-15b4f280ee3c.sketch_text.stroke-255"),sQuery(id+"F0.wireOp",EDGE,"46c11c21-c6ca-42b8-9659-15b4f280ee3c.sketch_text.stroke-256"),sQuery(id+"F0.wireOp",EDGE,"46c11c21-c6ca-42b8-9659-15b4f280ee3c.sketch_text.stroke-257"),sQuery(id+"F0.wireOp",EDGE,"46c11c21-c6ca-42b8-9659-15b4f280ee3c.sketch_text.stroke-258"),sQuery(id+"F0.wireOp",EDGE,"46c11c21-c6ca-42b8-9659-15b4f280ee3c.sketch_text.stroke-259"),sQuery(id+"F0.wireOp",EDGE,"46c11c21-c6ca-42b8-9659-15b4f280ee3c.sketch_text.stroke-260")])]});
            var Q6;
            Q6=makeQuery(id+"F1.opExtrude","SWEPT_BODY",BODY,{"disambiguationData":[OSD([sQuery(id+"F0.wireOp",EDGE,"46c11c21-c6ca-42b8-9659-15b4f280ee3c.sketch_text.stroke-230"),sQuery(id+"F0.wireOp",EDGE,"46c11c21-c6ca-42b8-9659-15b4f280ee3c.sketch_text.stroke-231"),sQuery(id+"F0.wireOp",EDGE,"46c11c21-c6ca-42b8-9659-15b4f280ee3c.sketch_text.stroke-232"),sQuery(id+"F0.wireOp",EDGE,"46c11c21-c6ca-42b8-9659-15b4f280ee3c.sketch_text.stroke-233"),sQuery(id+"F0.wireOp",EDGE,"46c11c21-c6ca-42b8-9659-15b4f280ee3c.sketch_text.stroke-234"),sQuery(id+"F0.wireOp",EDGE,"46c11c21-c6ca-42b8-9659-15b4f280ee3c.sketch_text.stroke-235"),sQuery(id+"F0.wireOp",EDGE,"46c11c21-c6ca-42b8-9659-15b4f280ee3c.sketch_text.stroke-236"),sQuery(id+"F0.wireOp",EDGE,"46c11c21-c6ca-42b8-9659-15b4f280ee3c.sketch_text.stroke-237"),sQuery(id+"F0.wireOp",EDGE,"46c11c21-c6ca-42b8-9659-15b4f280ee3c.sketch_text.stroke-238"),sQuery(id+"F0.wireOp",EDGE,"46c11c21-c6ca-42b8-9659-15b4f280ee3c.sketch_text.stroke-239"),sQuery(id+"F0.wireOp",EDGE,"46c11c21-c6ca-42b8-9659-15b4f280ee3c.sketch_text.stroke-240"),sQuery(id+"F0.wireOp",EDGE,"46c11c21-c6ca-42b8-9659-15b4f280ee3c.sketch_text.stroke-241")])]});
            var Q7;
            Q7=makeQuery(id+"F1.opExtrude","SWEPT_BODY",BODY,{"disambiguationData":[OSD([sQuery(id+"F0.wireOp",EDGE,"46c11c21-c6ca-42b8-9659-15b4f280ee3c.sketch_text.stroke-218"),sQuery(id+"F0.wireOp",EDGE,"46c11c21-c6ca-42b8-9659-15b4f280ee3c.sketch_text.stroke-219"),sQuery(id+"F0.wireOp",EDGE,"46c11c21-c6ca-42b8-9659-15b4f280ee3c.sketch_text.stroke-220"),sQuery(id+"F0.wireOp",EDGE,"46c11c21-c6ca-42b8-9659-15b4f280ee3c.sketch_text.stroke-221"),sQuery(id+"F0.wireOp",EDGE,"46c11c21-c6ca-42b8-9659-15b4f280ee3c.sketch_text.stroke-222"),sQuery(id+"F0.wireOp",EDGE,"46c11c21-c6ca-42b8-9659-15b4f280ee3c.sketch_text.stroke-223")])]});
            var Q8;
            Q8=makeQuery(id+"F1.opExtrude","SWEPT_BODY",BODY,{"disambiguationData":[OSD([sQuery(id+"F0.wireOp",EDGE,"46c11c21-c6ca-42b8-9659-15b4f280ee3c.sketch_text.stroke-204"),sQuery(id+"F0.wireOp",EDGE,"46c11c21-c6ca-42b8-9659-15b4f280ee3c.sketch_text.stroke-205"),sQuery(id+"F0.wireOp",EDGE,"46c11c21-c6ca-42b8-9659-15b4f280ee3c.sketch_text.stroke-206"),sQuery(id+"F0.wireOp",EDGE,"46c11c21-c6ca-42b8-9659-15b4f280ee3c.sketch_text.stroke-207"),sQuery(id+"F0.wireOp",EDGE,"46c11c21-c6ca-42b8-9659-15b4f280ee3c.sketch_text.stroke-208"),sQuery(id+"F0.wireOp",EDGE,"46c11c21-c6ca-42b8-9659-15b4f280ee3c.sketch_text.stroke-209"),sQuery(id+"F0.wireOp",EDGE,"46c11c21-c6ca-42b8-9659-15b4f280ee3c.sketch_text.stroke-210"),sQuery(id+"F0.wireOp",EDGE,"46c11c21-c6ca-42b8-9659-15b4f280ee3c.sketch_text.stroke-211"),sQuery(id+"F0.wireOp",EDGE,"46c11c21-c6ca-42b8-9659-15b4f280ee3c.sketch_text.stroke-212"),sQuery(id+"F0.wireOp",EDGE,"46c11c21-c6ca-42b8-9659-15b4f280ee3c.sketch_text.stroke-213"),sQuery(id+"F0.wireOp",EDGE,"46c11c21-c6ca-42b8-9659-15b4f280ee3c.sketch_text.stroke-214"),sQuery(id+"F0.wireOp",EDGE,"46c11c21-c6ca-42b8-9659-15b4f280ee3c.sketch_text.stroke-215"),sQuery(id+"F0.wireOp",EDGE,"46c11c21-c6ca-42b8-9659-15b4f280ee3c.sketch_text.stroke-216"),sQuery(id+"F0.wireOp",EDGE,"46c11c21-c6ca-42b8-9659-15b4f280ee3c.sketch_text.stroke-217")])]});
            var Q9;
            Q9=makeQuery(id+"F1.opExtrude","SWEPT_BODY",BODY,{"disambiguationData":[OSD([sQuery(id+"F0.wireOp",EDGE,"46c11c21-c6ca-42b8-9659-15b4f280ee3c.sketch_text.stroke-29"),sQuery(id+"F0.wireOp",EDGE,"46c11c21-c6ca-42b8-9659-15b4f280ee3c.sketch_text.stroke-30"),sQuery(id+"F0.wireOp",EDGE,"46c11c21-c6ca-42b8-9659-15b4f280ee3c.sketch_text.stroke-31"),sQuery(id+"F0.wireOp",EDGE,"46c11c21-c6ca-42b8-9659-15b4f280ee3c.sketch_text.stroke-32"),sQuery(id+"F0.wireOp",EDGE,"46c11c21-c6ca-42b8-9659-15b4f280ee3c.sketch_text.stroke-33"),sQuery(id+"F0.wireOp",EDGE,"46c11c21-c6ca-42b8-9659-15b4f280ee3c.sketch_text.stroke-34"),sQuery(id+"F0.wireOp",EDGE,"46c11c21-c6ca-42b8-9659-15b4f280ee3c.sketch_text.stroke-35"),sQuery(id+"F0.wireOp",EDGE,"46c11c21-c6ca-42b8-9659-15b4f280ee3c.sketch_text.stroke-36"),sQuery(id+"F0.wireOp",EDGE,"46c11c21-c6ca-42b8-9659-15b4f280ee3c.sketch_text.stroke-37"),sQuery(id+"F0.wireOp",EDGE,"46c11c21-c6ca-42b8-9659-15b4f280ee3c.sketch_text.stroke-38"),sQuery(id+"F0.wireOp",EDGE,"46c11c21-c6ca-42b8-9659-15b4f280ee3c.sketch_text.stroke-39"),sQuery(id+"F0.wireOp",EDGE,"46c11c21-c6ca-42b8-9659-15b4f280ee3c.sketch_text.stroke-40"),sQuery(id+"F0.wireOp",EDGE,"46c11c21-c6ca-42b8-9659-15b4f280ee3c.sketch_text.stroke-41"),sQuery(id+"F0.wireOp",EDGE,"46c11c21-c6ca-42b8-9659-15b4f280ee3c.sketch_text.stroke-42"),sQuery(id+"F0.wireOp",EDGE,"46c11c21-c6ca-42b8-9659-15b4f280ee3c.sketch_text.stroke-43"),sQuery(id+"F0.wireOp",EDGE,"46c11c21-c6ca-42b8-9659-15b4f280ee3c.sketch_text.stroke-44"),sQuery(id+"F0.wireOp",EDGE,"46c11c21-c6ca-42b8-9659-15b4f280ee3c.sketch_text.stroke-45"),sQuery(id+"F0.wireOp",EDGE,"46c11c21-c6ca-42b8-9659-15b4f280ee3c.sketch_text.stroke-46"),sQuery(id+"F0.wireOp",EDGE,"46c11c21-c6ca-42b8-9659-15b4f280ee3c.sketch_text.stroke-47")])]});
            var Q10;
            Q10=makeQuery(id+"F1.opExtrude","SWEPT_BODY",BODY,{"disambiguationData":[OSD([sQuery(id+"F0.wireOp",EDGE,"46c11c21-c6ca-42b8-9659-15b4f280ee3c.sketch_text.stroke-15"),sQuery(id+"F0.wireOp",EDGE,"46c11c21-c6ca-42b8-9659-15b4f280ee3c.sketch_text.stroke-16"),sQuery(id+"F0.wireOp",EDGE,"46c11c21-c6ca-42b8-9659-15b4f280ee3c.sketch_text.stroke-17"),sQuery(id+"F0.wireOp",EDGE,"46c11c21-c6ca-42b8-9659-15b4f280ee3c.sketch_text.stroke-18"),sQuery(id+"F0.wireOp",EDGE,"46c11c21-c6ca-42b8-9659-15b4f280ee3c.sketch_text.stroke-19"),sQuery(id+"F0.wireOp",EDGE,"46c11c21-c6ca-42b8-9659-15b4f280ee3c.sketch_text.stroke-20"),sQuery(id+"F0.wireOp",EDGE,"46c11c21-c6ca-42b8-9659-15b4f280ee3c.sketch_text.stroke-21"),sQuery(id+"F0.wireOp",EDGE,"46c11c21-c6ca-42b8-9659-15b4f280ee3c.sketch_text.stroke-22"),sQuery(id+"F0.wireOp",EDGE,"46c11c21-c6ca-42b8-9659-15b4f280ee3c.sketch_text.stroke-23"),sQuery(id+"F0.wireOp",EDGE,"46c11c21-c6ca-42b8-9659-15b4f280ee3c.sketch_text.stroke-24"),sQuery(id+"F0.wireOp",EDGE,"46c11c21-c6ca-42b8-9659-15b4f280ee3c.sketch_text.stroke-25"),sQuery(id+"F0.wireOp",EDGE,"46c11c21-c6ca-42b8-9659-15b4f280ee3c.sketch_text.stroke-26"),sQuery(id+"F0.wireOp",EDGE,"46c11c21-c6ca-42b8-9659-15b4f280ee3c.sketch_text.stroke-27"),sQuery(id+"F0.wireOp",EDGE,"46c11c21-c6ca-42b8-9659-15b4f280ee3c.sketch_text.stroke-28")])]});
            var Q11;
            Q11=makeQuery(id+"F1.opExtrude","SWEPT_BODY",BODY,{"disambiguationData":[OSD([sQuery(id+"F0.wireOp",EDGE,"E3"),sQuery(id+"F0.wireOp",EDGE,"E4"),sQuery(id+"F0.wireOp",EDGE,"E5"),sQuery(id+"F0.wireOp",EDGE,"E6.0"),sQuery(id+"F0.wireOp",EDGE,"E6.1"),sQuery(id+"F0.wireOp",EDGE,"E6.2"),sQuery(id+"F0.wireOp",EDGE,"E9.filletArc"),sQuery(id+"F0.wireOp",EDGE,"E10.filletArc"),sQuery(id+"F0.wireOp",EDGE,"E12.6.MirrorCS"),sQuery(id+"F0.wireOp",EDGE,"E12.7.MirrorCS"),sQuery(id+"F0.wireOp",EDGE,"E12.8.MirrorCS"),sQuery(id+"F0.wireOp",EDGE,"E12.10.MirrorCS"),sQuery(id+"F0.wireOp",EDGE,"E12.12.MirrorCS"),sQuery(id+"F0.wireOp",EDGE,"E12.13.MirrorCS"),sQuery(id+"F0.wireOp",EDGE,"E12.14.MirrorCS"),sQuery(id+"F0.wireOp",EDGE,"E12.15.MirrorCS"),sQuery(id+"F0.wireOp",EDGE,"E29.filletArc"),sQuery(id+"F0.wireOp",EDGE,"E30.filletArc"),sQuery(id+"F0.wireOp",EDGE,"E31.filletArc"),sQuery(id+"F0.wireOp",EDGE,"E32.filletArc"),sQuery(id+"F0.wireOp",EDGE,"E33.filletArc"),sQuery(id+"F0.wireOp",EDGE,"E34.filletArc"),sQuery(id+"F0.wireOp",EDGE,"E35.filletArc"),sQuery(id+"F0.wireOp",EDGE,"E36.filletArc"),sQuery(id+"F0.wireOp",EDGE,"E37.filletArc"),sQuery(id+"F0.wireOp",EDGE,"E38.filletArc")])]});
            var Q12;
            Q12=makeQuery(id+"F1.opExtrude","SWEPT_BODY",BODY,{"disambiguationData":[OSD([sQuery(id+"F0.wireOp",EDGE,"E12.1.MirrorCS"),sQuery(id+"F0.wireOp",EDGE,"E12.3.MirrorCS"),sQuery(id+"F0.wireOp",EDGE,"E12.4.MirrorCS"),sQuery(id+"F0.wireOp",EDGE,"E12.5.MirrorCS"),sQuery(id+"F0.wireOp",EDGE,"E21.filletArc"),sQuery(id+"F0.wireOp",EDGE,"E22.filletArc"),sQuery(id+"F0.wireOp",EDGE,"E23.filletArc"),sQuery(id+"F0.wireOp",EDGE,"E24.filletArc")])]});
            var Q13;
            Q13=makeQuery(id+"F1.opExtrude","SWEPT_BODY",BODY,{"disambiguationData":[OSD([sQuery(id+"F0.wireOp",EDGE,"E41"),sQuery(id+"F0.wireOp",EDGE,"E42"),sQuery(id+"F0.wireOp",EDGE,"E43"),sQuery(id+"F0.wireOp",EDGE,"E54.trimOffspring")])]});
            var Q14;
            Q14=makeQuery(id+"F1.opExtrude","SWEPT_BODY",BODY,{"disambiguationData":[OSD([sQuery(id+"F0.wireOp",EDGE,"46c11c21-c6ca-42b8-9659-15b4f280ee3c.sketch_text.stroke-163"),sQuery(id+"F0.wireOp",EDGE,"46c11c21-c6ca-42b8-9659-15b4f280ee3c.sketch_text.stroke-164"),sQuery(id+"F0.wireOp",EDGE,"46c11c21-c6ca-42b8-9659-15b4f280ee3c.sketch_text.stroke-165"),sQuery(id+"F0.wireOp",EDGE,"46c11c21-c6ca-42b8-9659-15b4f280ee3c.sketch_text.stroke-166"),sQuery(id+"F0.wireOp",EDGE,"46c11c21-c6ca-42b8-9659-15b4f280ee3c.sketch_text.stroke-167"),sQuery(id+"F0.wireOp",EDGE,"46c11c21-c6ca-42b8-9659-15b4f280ee3c.sketch_text.stroke-168"),sQuery(id+"F0.wireOp",EDGE,"46c11c21-c6ca-42b8-9659-15b4f280ee3c.sketch_text.stroke-169"),sQuery(id+"F0.wireOp",EDGE,"46c11c21-c6ca-42b8-9659-15b4f280ee3c.sketch_text.stroke-170"),sQuery(id+"F0.wireOp",EDGE,"46c11c21-c6ca-42b8-9659-15b4f280ee3c.sketch_text.stroke-171"),sQuery(id+"F0.wireOp",EDGE,"46c11c21-c6ca-42b8-9659-15b4f280ee3c.sketch_text.stroke-172"),sQuery(id+"F0.wireOp",EDGE,"46c11c21-c6ca-42b8-9659-15b4f280ee3c.sketch_text.stroke-173"),sQuery(id+"F0.wireOp",EDGE,"46c11c21-c6ca-42b8-9659-15b4f280ee3c.sketch_text.stroke-174"),sQuery(id+"F0.wireOp",EDGE,"46c11c21-c6ca-42b8-9659-15b4f280ee3c.sketch_text.stroke-175"),sQuery(id+"F0.wireOp",EDGE,"46c11c21-c6ca-42b8-9659-15b4f280ee3c.sketch_text.stroke-176")])]});
            var Q15;
            Q15=makeQuery(id+"F1.opExtrude","SWEPT_BODY",BODY,{"disambiguationData":[OSD([sQuery(id+"F0.wireOp",EDGE,"46c11c21-c6ca-42b8-9659-15b4f280ee3c.sketch_text.stroke-115"),sQuery(id+"F0.wireOp",EDGE,"46c11c21-c6ca-42b8-9659-15b4f280ee3c.sketch_text.stroke-116"),sQuery(id+"F0.wireOp",EDGE,"46c11c21-c6ca-42b8-9659-15b4f280ee3c.sketch_text.stroke-117"),sQuery(id+"F0.wireOp",EDGE,"46c11c21-c6ca-42b8-9659-15b4f280ee3c.sketch_text.stroke-118"),sQuery(id+"F0.wireOp",EDGE,"46c11c21-c6ca-42b8-9659-15b4f280ee3c.sketch_text.stroke-119"),sQuery(id+"F0.wireOp",EDGE,"46c11c21-c6ca-42b8-9659-15b4f280ee3c.sketch_text.stroke-120"),sQuery(id+"F0.wireOp",EDGE,"46c11c21-c6ca-42b8-9659-15b4f280ee3c.sketch_text.stroke-121"),sQuery(id+"F0.wireOp",EDGE,"46c11c21-c6ca-42b8-9659-15b4f280ee3c.sketch_text.stroke-122"),sQuery(id+"F0.wireOp",EDGE,"46c11c21-c6ca-42b8-9659-15b4f280ee3c.sketch_text.stroke-123"),sQuery(id+"F0.wireOp",EDGE,"46c11c21-c6ca-42b8-9659-15b4f280ee3c.sketch_text.stroke-124"),sQuery(id+"F0.wireOp",EDGE,"46c11c21-c6ca-42b8-9659-15b4f280ee3c.sketch_text.stroke-125"),sQuery(id+"F0.wireOp",EDGE,"46c11c21-c6ca-42b8-9659-15b4f280ee3c.sketch_text.stroke-126"),sQuery(id+"F0.wireOp",EDGE,"46c11c21-c6ca-42b8-9659-15b4f280ee3c.sketch_text.stroke-127"),sQuery(id+"F0.wireOp",EDGE,"46c11c21-c6ca-42b8-9659-15b4f280ee3c.sketch_text.stroke-128"),sQuery(id+"F0.wireOp",EDGE,"46c11c21-c6ca-42b8-9659-15b4f280ee3c.sketch_text.stroke-129"),sQuery(id+"F0.wireOp",EDGE,"46c11c21-c6ca-42b8-9659-15b4f280ee3c.sketch_text.stroke-130"),sQuery(id+"F0.wireOp",EDGE,"46c11c21-c6ca-42b8-9659-15b4f280ee3c.sketch_text.stroke-131"),sQuery(id+"F0.wireOp",EDGE,"46c11c21-c6ca-42b8-9659-15b4f280ee3c.sketch_text.stroke-132"),sQuery(id+"F0.wireOp",EDGE,"46c11c21-c6ca-42b8-9659-15b4f280ee3c.sketch_text.stroke-133")])]});
            var Q16;
            Q16=makeQuery(id+"F1.opExtrude","SWEPT_BODY",BODY,{"disambiguationData":[OSD([sQuery(id+"F0.wireOp",EDGE,"46c11c21-c6ca-42b8-9659-15b4f280ee3c.sketch_text.stroke-185"),sQuery(id+"F0.wireOp",EDGE,"46c11c21-c6ca-42b8-9659-15b4f280ee3c.sketch_text.stroke-186"),sQuery(id+"F0.wireOp",EDGE,"46c11c21-c6ca-42b8-9659-15b4f280ee3c.sketch_text.stroke-187"),sQuery(id+"F0.wireOp",EDGE,"46c11c21-c6ca-42b8-9659-15b4f280ee3c.sketch_text.stroke-188"),sQuery(id+"F0.wireOp",EDGE,"46c11c21-c6ca-42b8-9659-15b4f280ee3c.sketch_text.stroke-189"),sQuery(id+"F0.wireOp",EDGE,"46c11c21-c6ca-42b8-9659-15b4f280ee3c.sketch_text.stroke-190"),sQuery(id+"F0.wireOp",EDGE,"46c11c21-c6ca-42b8-9659-15b4f280ee3c.sketch_text.stroke-191"),sQuery(id+"F0.wireOp",EDGE,"46c11c21-c6ca-42b8-9659-15b4f280ee3c.sketch_text.stroke-192"),sQuery(id+"F0.wireOp",EDGE,"46c11c21-c6ca-42b8-9659-15b4f280ee3c.sketch_text.stroke-193"),sQuery(id+"F0.wireOp",EDGE,"46c11c21-c6ca-42b8-9659-15b4f280ee3c.sketch_text.stroke-194"),sQuery(id+"F0.wireOp",EDGE,"46c11c21-c6ca-42b8-9659-15b4f280ee3c.sketch_text.stroke-195"),sQuery(id+"F0.wireOp",EDGE,"46c11c21-c6ca-42b8-9659-15b4f280ee3c.sketch_text.stroke-196"),sQuery(id+"F0.wireOp",EDGE,"46c11c21-c6ca-42b8-9659-15b4f280ee3c.sketch_text.stroke-197"),sQuery(id+"F0.wireOp",EDGE,"46c11c21-c6ca-42b8-9659-15b4f280ee3c.sketch_text.stroke-198"),sQuery(id+"F0.wireOp",EDGE,"46c11c21-c6ca-42b8-9659-15b4f280ee3c.sketch_text.stroke-199"),sQuery(id+"F0.wireOp",EDGE,"46c11c21-c6ca-42b8-9659-15b4f280ee3c.sketch_text.stroke-200"),sQuery(id+"F0.wireOp",EDGE,"46c11c21-c6ca-42b8-9659-15b4f280ee3c.sketch_text.stroke-201"),sQuery(id+"F0.wireOp",EDGE,"46c11c21-c6ca-42b8-9659-15b4f280ee3c.sketch_text.stroke-202"),sQuery(id+"F0.wireOp",EDGE,"46c11c21-c6ca-42b8-9659-15b4f280ee3c.sketch_text.stroke-203")])]});
            var Q17;
            Q17=makeQuery(id+"F1.opExtrude","SWEPT_BODY",BODY,{"disambiguationData":[OSD([sQuery(id+"F0.wireOp",EDGE,"E46.trimOffspring"),sQuery(id+"F0.wireOp",EDGE,"E48.trimOffspring"),sQuery(id+"F0.wireOp",EDGE,"E51.trimOffspring"),sQuery(id+"F0.wireOp",EDGE,"E53.trimOffspring")])]});
            var Q18;
            Q18=makeQuery(id+"F1.opExtrude","SWEPT_BODY",BODY,{"disambiguationData":[OSD([sQuery(id+"F0.wireOp",EDGE,"E11.right"),sQuery(id+"F0.wireOp",EDGE,"E11.left"),sQuery(id+"F0.wireOp",EDGE,"E11.top"),sQuery(id+"F0.wireOp",EDGE,"E11.bottom"),sQuery(id+"F0.wireOp",EDGE,"E25.filletArc"),sQuery(id+"F0.wireOp",EDGE,"E26.filletArc"),sQuery(id+"F0.wireOp",EDGE,"E27.filletArc"),sQuery(id+"F0.wireOp",EDGE,"E28.filletArc")])]});
            var Q19;
            Q19=makeQuery(id+"F1.opExtrude","SWEPT_BODY",BODY,{"disambiguationData":[OSD([sQuery(id+"F0.wireOp",EDGE,"46c11c21-c6ca-42b8-9659-15b4f280ee3c.sketch_text.stroke-224"),sQuery(id+"F0.wireOp",EDGE,"46c11c21-c6ca-42b8-9659-15b4f280ee3c.sketch_text.stroke-225"),sQuery(id+"F0.wireOp",EDGE,"46c11c21-c6ca-42b8-9659-15b4f280ee3c.sketch_text.stroke-226"),sQuery(id+"F0.wireOp",EDGE,"46c11c21-c6ca-42b8-9659-15b4f280ee3c.sketch_text.stroke-227"),sQuery(id+"F0.wireOp",EDGE,"46c11c21-c6ca-42b8-9659-15b4f280ee3c.sketch_text.stroke-228"),sQuery(id+"F0.wireOp",EDGE,"46c11c21-c6ca-42b8-9659-15b4f280ee3c.sketch_text.stroke-229")])]});
            var Q20;
            Q20=makeQuery(id+"F1.opExtrude","SWEPT_BODY",BODY,{"disambiguationData":[OSD([sQuery(id+"F0.wireOp",EDGE,"46c11c21-c6ca-42b8-9659-15b4f280ee3c.sketch_text.stroke-60"),sQuery(id+"F0.wireOp",EDGE,"46c11c21-c6ca-42b8-9659-15b4f280ee3c.sketch_text.stroke-61"),sQuery(id+"F0.wireOp",EDGE,"46c11c21-c6ca-42b8-9659-15b4f280ee3c.sketch_text.stroke-62"),sQuery(id+"F0.wireOp",EDGE,"46c11c21-c6ca-42b8-9659-15b4f280ee3c.sketch_text.stroke-63"),sQuery(id+"F0.wireOp",EDGE,"46c11c21-c6ca-42b8-9659-15b4f280ee3c.sketch_text.stroke-64"),sQuery(id+"F0.wireOp",EDGE,"46c11c21-c6ca-42b8-9659-15b4f280ee3c.sketch_text.stroke-65"),sQuery(id+"F0.wireOp",EDGE,"46c11c21-c6ca-42b8-9659-15b4f280ee3c.sketch_text.stroke-66"),sQuery(id+"F0.wireOp",EDGE,"46c11c21-c6ca-42b8-9659-15b4f280ee3c.sketch_text.stroke-67"),sQuery(id+"F0.wireOp",EDGE,"46c11c21-c6ca-42b8-9659-15b4f280ee3c.sketch_text.stroke-68"),sQuery(id+"F0.wireOp",EDGE,"46c11c21-c6ca-42b8-9659-15b4f280ee3c.sketch_text.stroke-69"),sQuery(id+"F0.wireOp",EDGE,"46c11c21-c6ca-42b8-9659-15b4f280ee3c.sketch_text.stroke-70"),sQuery(id+"F0.wireOp",EDGE,"46c11c21-c6ca-42b8-9659-15b4f280ee3c.sketch_text.stroke-71"),sQuery(id+"F0.wireOp",EDGE,"46c11c21-c6ca-42b8-9659-15b4f280ee3c.sketch_text.stroke-72"),sQuery(id+"F0.wireOp",EDGE,"46c11c21-c6ca-42b8-9659-15b4f280ee3c.sketch_text.stroke-73"),sQuery(id+"F0.wireOp",EDGE,"46c11c21-c6ca-42b8-9659-15b4f280ee3c.sketch_text.stroke-74"),sQuery(id+"F0.wireOp",EDGE,"46c11c21-c6ca-42b8-9659-15b4f280ee3c.sketch_text.stroke-75"),sQuery(id+"F0.wireOp",EDGE,"46c11c21-c6ca-42b8-9659-15b4f280ee3c.sketch_text.stroke-76"),sQuery(id+"F0.wireOp",EDGE,"46c11c21-c6ca-42b8-9659-15b4f280ee3c.sketch_text.stroke-77"),sQuery(id+"F0.wireOp",EDGE,"46c11c21-c6ca-42b8-9659-15b4f280ee3c.sketch_text.stroke-78")])]});
            var Q21;
            Q21=makeQuery(id+"F1.opExtrude","SWEPT_BODY",BODY,{"disambiguationData":[OSD([sQuery(id+"F0.wireOp",EDGE,"E39"),sQuery(id+"F0.wireOp",EDGE,"E40"),sQuery(id+"F0.wireOp",EDGE,"E44.trimOffspring"),sQuery(id+"F0.wireOp",EDGE,"E52.trimOffspring")])]});
            var Q22;
            Q22=makeQuery(id+"F1.opExtrude","SWEPT_BODY",BODY,{"disambiguationData":[OSD([sQuery(id+"F0.wireOp",EDGE,"46c11c21-c6ca-42b8-9659-15b4f280ee3c.sketch_text.stroke-177"),sQuery(id+"F0.wireOp",EDGE,"46c11c21-c6ca-42b8-9659-15b4f280ee3c.sketch_text.stroke-178"),sQuery(id+"F0.wireOp",EDGE,"46c11c21-c6ca-42b8-9659-15b4f280ee3c.sketch_text.stroke-179"),sQuery(id+"F0.wireOp",EDGE,"46c11c21-c6ca-42b8-9659-15b4f280ee3c.sketch_text.stroke-180"),sQuery(id+"F0.wireOp",EDGE,"46c11c21-c6ca-42b8-9659-15b4f280ee3c.sketch_text.stroke-181"),sQuery(id+"F0.wireOp",EDGE,"46c11c21-c6ca-42b8-9659-15b4f280ee3c.sketch_text.stroke-182"),sQuery(id+"F0.wireOp",EDGE,"46c11c21-c6ca-42b8-9659-15b4f280ee3c.sketch_text.stroke-183"),sQuery(id+"F0.wireOp",EDGE,"46c11c21-c6ca-42b8-9659-15b4f280ee3c.sketch_text.stroke-184")])]});
            var Q23;
            Q23=makeQuery(id+"F1.opExtrude","SWEPT_BODY",BODY,{"disambiguationData":[OSD([sQuery(id+"F0.wireOp",EDGE,"46c11c21-c6ca-42b8-9659-15b4f280ee3c.sketch_text.stroke-0"),sQuery(id+"F0.wireOp",EDGE,"46c11c21-c6ca-42b8-9659-15b4f280ee3c.sketch_text.stroke-1"),sQuery(id+"F0.wireOp",EDGE,"46c11c21-c6ca-42b8-9659-15b4f280ee3c.sketch_text.stroke-2"),sQuery(id+"F0.wireOp",EDGE,"46c11c21-c6ca-42b8-9659-15b4f280ee3c.sketch_text.stroke-3"),sQuery(id+"F0.wireOp",EDGE,"46c11c21-c6ca-42b8-9659-15b4f280ee3c.sketch_text.stroke-4"),sQuery(id+"F0.wireOp",EDGE,"46c11c21-c6ca-42b8-9659-15b4f280ee3c.sketch_text.stroke-5"),sQuery(id+"F0.wireOp",EDGE,"46c11c21-c6ca-42b8-9659-15b4f280ee3c.sketch_text.stroke-6"),sQuery(id+"F0.wireOp",EDGE,"46c11c21-c6ca-42b8-9659-15b4f280ee3c.sketch_text.stroke-7"),sQuery(id+"F0.wireOp",EDGE,"46c11c21-c6ca-42b8-9659-15b4f280ee3c.sketch_text.stroke-8"),sQuery(id+"F0.wireOp",EDGE,"46c11c21-c6ca-42b8-9659-15b4f280ee3c.sketch_text.stroke-9"),sQuery(id+"F0.wireOp",EDGE,"46c11c21-c6ca-42b8-9659-15b4f280ee3c.sketch_text.stroke-10"),sQuery(id+"F0.wireOp",EDGE,"46c11c21-c6ca-42b8-9659-15b4f280ee3c.sketch_text.stroke-11"),sQuery(id+"F0.wireOp",EDGE,"46c11c21-c6ca-42b8-9659-15b4f280ee3c.sketch_text.stroke-12"),sQuery(id+"F0.wireOp",EDGE,"46c11c21-c6ca-42b8-9659-15b4f280ee3c.sketch_text.stroke-13"),sQuery(id+"F0.wireOp",EDGE,"46c11c21-c6ca-42b8-9659-15b4f280ee3c.sketch_text.stroke-14")])]});
            var Q24;
            Q24=makeQuery(id+"F1.opExtrude","SWEPT_BODY",BODY,{"disambiguationData":[OSD([sQuery(id+"F0.wireOp",EDGE,"46c11c21-c6ca-42b8-9659-15b4f280ee3c.sketch_text.stroke-48"),sQuery(id+"F0.wireOp",EDGE,"46c11c21-c6ca-42b8-9659-15b4f280ee3c.sketch_text.stroke-49"),sQuery(id+"F0.wireOp",EDGE,"46c11c21-c6ca-42b8-9659-15b4f280ee3c.sketch_text.stroke-50"),sQuery(id+"F0.wireOp",EDGE,"46c11c21-c6ca-42b8-9659-15b4f280ee3c.sketch_text.stroke-51"),sQuery(id+"F0.wireOp",EDGE,"46c11c21-c6ca-42b8-9659-15b4f280ee3c.sketch_text.stroke-52"),sQuery(id+"F0.wireOp",EDGE,"46c11c21-c6ca-42b8-9659-15b4f280ee3c.sketch_text.stroke-53"),sQuery(id+"F0.wireOp",EDGE,"46c11c21-c6ca-42b8-9659-15b4f280ee3c.sketch_text.stroke-54"),sQuery(id+"F0.wireOp",EDGE,"46c11c21-c6ca-42b8-9659-15b4f280ee3c.sketch_text.stroke-55"),sQuery(id+"F0.wireOp",EDGE,"46c11c21-c6ca-42b8-9659-15b4f280ee3c.sketch_text.stroke-56"),sQuery(id+"F0.wireOp",EDGE,"46c11c21-c6ca-42b8-9659-15b4f280ee3c.sketch_text.stroke-57"),sQuery(id+"F0.wireOp",EDGE,"46c11c21-c6ca-42b8-9659-15b4f280ee3c.sketch_text.stroke-58"),sQuery(id+"F0.wireOp",EDGE,"46c11c21-c6ca-42b8-9659-15b4f280ee3c.sketch_text.stroke-59")])]});
            var Q25;
            Q25=makeQuery(id+"F1.opExtrude","SWEPT_BODY",BODY,{"disambiguationData":[OSD([sQuery(id+"F0.wireOp",EDGE,"46c11c21-c6ca-42b8-9659-15b4f280ee3c.sketch_text.stroke-93"),sQuery(id+"F0.wireOp",EDGE,"46c11c21-c6ca-42b8-9659-15b4f280ee3c.sketch_text.stroke-94"),sQuery(id+"F0.wireOp",EDGE,"46c11c21-c6ca-42b8-9659-15b4f280ee3c.sketch_text.stroke-95"),sQuery(id+"F0.wireOp",EDGE,"46c11c21-c6ca-42b8-9659-15b4f280ee3c.sketch_text.stroke-96"),sQuery(id+"F0.wireOp",EDGE,"46c11c21-c6ca-42b8-9659-15b4f280ee3c.sketch_text.stroke-97"),sQuery(id+"F0.wireOp",EDGE,"46c11c21-c6ca-42b8-9659-15b4f280ee3c.sketch_text.stroke-98"),sQuery(id+"F0.wireOp",EDGE,"46c11c21-c6ca-42b8-9659-15b4f280ee3c.sketch_text.stroke-99"),sQuery(id+"F0.wireOp",EDGE,"46c11c21-c6ca-42b8-9659-15b4f280ee3c.sketch_text.stroke-100")])]});
            var Q26;
            Q26=makeQuery(id+"F1.opExtrude","SWEPT_BODY",BODY,{"disambiguationData":[OSD([sQuery(id+"F0.wireOp",EDGE,"E1.bottom"),sQuery(id+"F0.wireOp",EDGE,"E1.top"),sQuery(id+"F0.wireOp",EDGE,"E1.left"),sQuery(id+"F0.wireOp",EDGE,"E1.right"),sQuery(id+"F0.wireOp",EDGE,"E13.filletArc"),sQuery(id+"F0.wireOp",EDGE,"E14.filletArc"),sQuery(id+"F0.wireOp",EDGE,"E15.filletArc"),sQuery(id+"F0.wireOp",EDGE,"E16.filletArc")])]});
            var Q27;
            Q27=makeQuery(id+"F1.opExtrude","SWEPT_BODY",BODY,{"disambiguationData":[OSD([sQuery(id+"F0.wireOp",EDGE,"E45"),sQuery(id+"F0.wireOp",EDGE,"E47"),sQuery(id+"F0.wireOp",EDGE,"E49.trimOffspring"),sQuery(id+"F0.wireOp",EDGE,"E50.trimOffspring")])]});
            var Q28;
            Q28=qCreatedBy(makeId("Origin.pointOp"),VERTEX);
            transform(context, id + "F2", {"entities" : qUnion([Q0, Q1, Q2, Q3, Q4, Q5, Q6, Q7, Q8, Q9, Q10, Q11, Q12, Q13, Q14, Q15, Q16, Q17, Q18, Q19, Q20, Q21, Q22, Q23, Q24, Q25, Q26, Q27]), "transformType" : TransformType.SCALE_UNIFORMLY, "scale" : .357, "makeCopy" : false, "scalePoint" : qUnion([Q28])});
        }
        {
            var Q0;
            Q0=qCreatedBy(makeId("Top.planeOp"),FACE);
            var sketch = newSketch(context, id + "F3", { "sketchPlane" : qUnion([Q0])});
            skText(sketch, "E55", { "text": "C O R E   S E R V O\nC O N T R O L L E R", "fontName": "Arimo-Bold.ttf"});
            const initialGuessF3  = {"E55": [-0.0235, -0.0035, 1, 0, 0.0025]};
            skSetInitialGuess(sketch, initialGuessF3);
            skSolve(sketch);
        }
        {
            var Q0;
            Q0=qSketchRegion(id+"F3",true);
            extrude(context, id + "F4", {"entities" : qUnion([Q0]), "depth" : .1 * mm});
        }
    });
